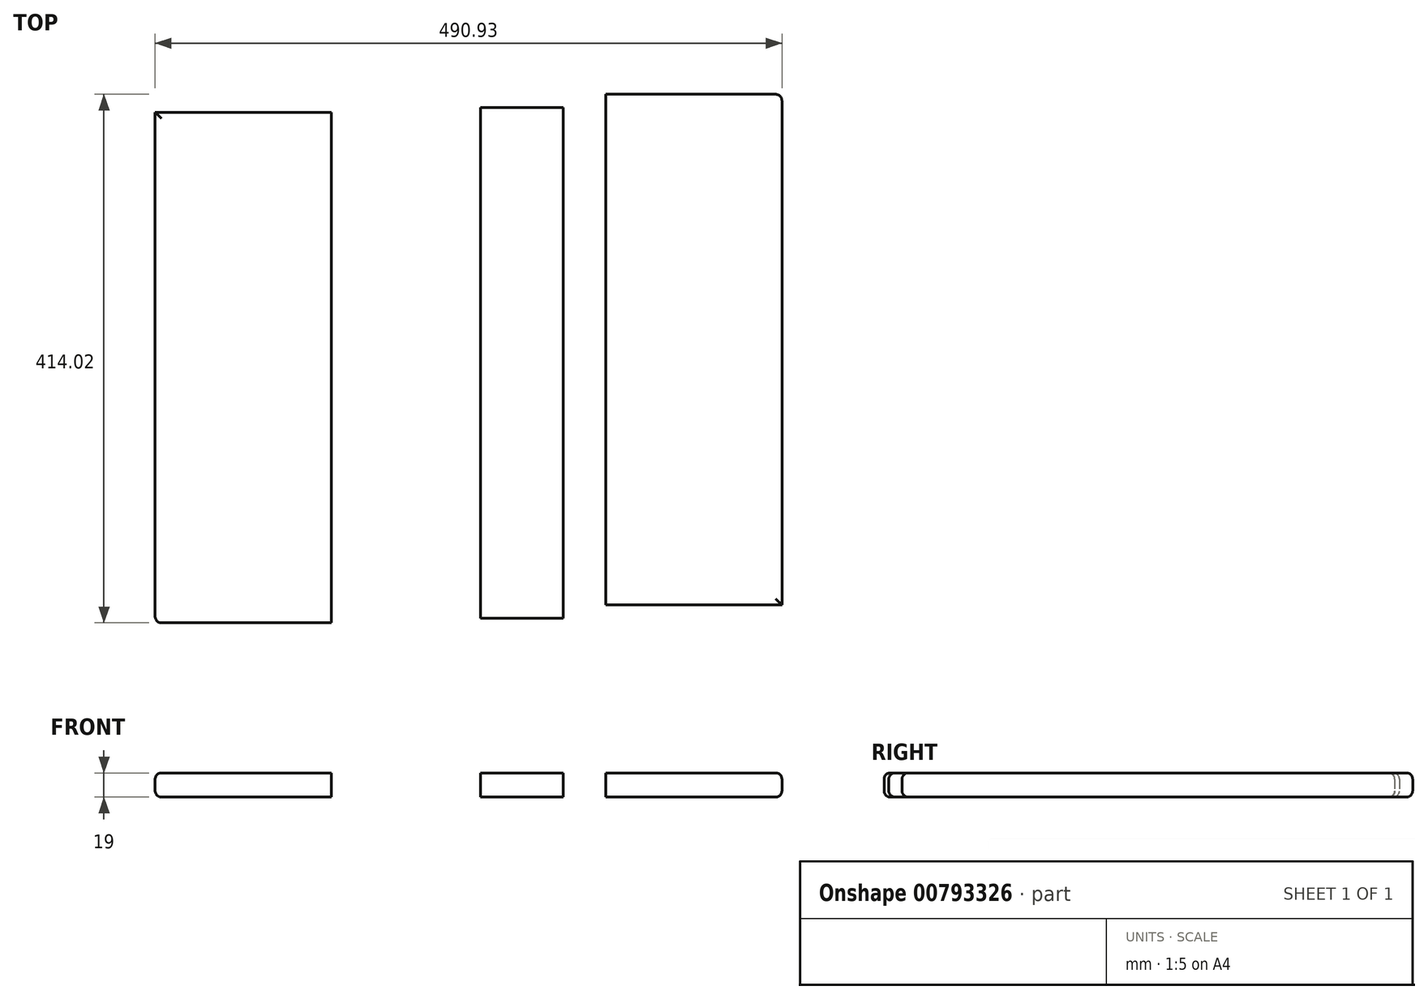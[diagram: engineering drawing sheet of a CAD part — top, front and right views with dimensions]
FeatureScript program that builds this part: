
annotation { "Feature Type Name" : "Feature", "Feature Type Description" : "" }
export const myFeature = defineFeature(function(context is Context, id is Id, definition is map)
    precondition{}
    {
        {
            var Q0;
            Q0=qCreatedBy(makeId("Top.planeOp"),FACE);
            var sketch = newSketch(context, id + "F0", { "sketchPlane" : qUnion([Q0])});
            skLineSegment(sketch, "E0.bottom", {"start": v(-196.42, 329.78) * mm, "end": v(-58.42, 329.78) * mm});
            skLineSegment(sketch, "E0.top", {"start": v(-196.42, -70.22) * mm, "end": v(-58.42, -70.22) * mm});
            skLineSegment(sketch, "E0.left", {"start": v(-196.42, 329.78) * mm, "end": v(-196.42, -70.22) * mm});
            skLineSegment(sketch, "E0.right", {"start": v(-58.42, 329.78) * mm, "end": v(-58.42, -70.22) * mm});
            skLineSegment(sketch, "E1.bottom", {"start": v(58.32, 333.43) * mm, "end": v(123.32, 333.43) * mm});
            skLineSegment(sketch, "E1.top", {"start": v(58.32, -66.57) * mm, "end": v(123.32, -66.57) * mm});
            skLineSegment(sketch, "E1.left", {"start": v(58.32, 333.43) * mm, "end": v(58.32, -66.57) * mm});
            skLineSegment(sketch, "E1.right", {"start": v(123.32, 333.43) * mm, "end": v(123.32, -66.57) * mm});
            skLineSegment(sketch, "E2.bottom", {"start": v(156.5, 343.8) * mm, "end": v(294.5, 343.8) * mm});
            skLineSegment(sketch, "E2.top", {"start": v(156.5, -56.2) * mm, "end": v(294.5, -56.2) * mm});
            skLineSegment(sketch, "E2.left", {"start": v(156.5, 343.8) * mm, "end": v(156.5, -56.2) * mm});
            skLineSegment(sketch, "E2.right", {"start": v(294.5, 343.8) * mm, "end": v(294.5, -56.2) * mm});
            skSolve(sketch);
        }
        {
            var Q0;
            Q0=makeQuery(id+"F0.imprint","IMPRINT",FACE,{"disambiguationData":[TD([[makeQuery(id+"F0.imprint","IMPRINT",EDGE,{"derivedFrom":sQuery(id+"F0.wireOp",EDGE,"E0.bottom")}),-1.0]])]});
            var Q1;
            Q1=makeQuery(id+"F0.imprint","IMPRINT",FACE,{"disambiguationData":[TD([[makeQuery(id+"F0.imprint","IMPRINT",EDGE,{"derivedFrom":sQuery(id+"F0.wireOp",EDGE,"E1.bottom")}),-1.0]])]});
            var Q2;
            Q2=makeQuery(id+"F0.imprint","IMPRINT",FACE,{"disambiguationData":[TD([[makeQuery(id+"F0.imprint","IMPRINT",EDGE,{"derivedFrom":sQuery(id+"F0.wireOp",EDGE,"E2.bottom")}),-1.0]])]});
            extrude(context, id + "F1", {"entities" : qUnion([Q0, Q1, Q2]), "depth" : 19 * mm, "offsetDistance" : 25 * mm});
        }
        {
            var Q0;
            Q0=makeQuery(id+"F1.opExtrude","CAP_EDGE",EDGE,{"disambiguationData":[OSD([sQuery(id+"F0.wireOp",EDGE,"E0.left")])],"isStart":false});
            var Q1;
            Q1=makeQuery(id+"F1.opExtrude","CAP_EDGE",EDGE,{"disambiguationData":[OSD([sQuery(id+"F0.wireOp",EDGE,"E0.bottom")])],"isStart":false});
            var Q2;
            Q2=makeQuery(id+"F1.opExtrude","CAP_EDGE",EDGE,{"disambiguationData":[OSD([sQuery(id+"F0.wireOp",EDGE,"E1.bottom")])],"isStart":false});
            var Q3;
            Q3=makeQuery(id+"F1.opExtrude","CAP_EDGE",EDGE,{"disambiguationData":[OSD([sQuery(id+"F0.wireOp",EDGE,"E2.bottom")])],"isStart":false});
            var Q4;
            Q4=makeQuery(id+"F1.opExtrude","CAP_EDGE",EDGE,{"disambiguationData":[OSD([sQuery(id+"F0.wireOp",EDGE,"E2.right")])],"isStart":true});
            var Q5;
            Q5=makeQuery(id+"F1.opExtrude","CAP_EDGE",EDGE,{"disambiguationData":[OSD([sQuery(id+"F0.wireOp",EDGE,"E2.top")])],"isStart":true});
            var Q6;
            Q6=makeQuery(id+"F1.opExtrude","CAP_EDGE",EDGE,{"disambiguationData":[OSD([sQuery(id+"F0.wireOp",EDGE,"E1.top")])],"isStart":true});
            var Q7;
            Q7=makeQuery(id+"F1.opExtrude","CAP_EDGE",EDGE,{"disambiguationData":[OSD([sQuery(id+"F0.wireOp",EDGE,"E0.top")])],"isStart":true});
            fillet(context, id + "F2", {"entities" : qUnion([Q0, Q1, Q2, Q3, Q4, Q5, Q6, Q7]), "radius" : 5 * mm, "tangentPropagation" : true, "allowEdgeOverflow" : false});
        }
        {
            var Q0;
            Q0=makeQuery(id+"F1.opExtrude","CAP_EDGE",EDGE,{"disambiguationData":[OSD([sQuery(id+"F0.wireOp",EDGE,"E0.top")])],"isStart":false});
            var Q1;
            Q1=makeQuery(id+"F1.opExtrude","CAP_EDGE",EDGE,{"disambiguationData":[OSD([sQuery(id+"F0.wireOp",EDGE,"E0.left")])],"isStart":true});
            var Q2;
            Q2=makeQuery(id+"F1.opExtrude","CAP_EDGE",EDGE,{"disambiguationData":[OSD([sQuery(id+"F0.wireOp",EDGE,"E0.bottom")])],"isStart":true});
            var Q3;
            Q3=makeQuery(id+"F1.opExtrude","CAP_EDGE",EDGE,{"disambiguationData":[OSD([sQuery(id+"F0.wireOp",EDGE,"E1.bottom")])],"isStart":true});
            var Q4;
            Q4=makeQuery(id+"F1.opExtrude","CAP_EDGE",EDGE,{"disambiguationData":[OSD([sQuery(id+"F0.wireOp",EDGE,"E1.top")])],"isStart":false});
            var Q5;
            Q5=makeQuery(id+"F1.opExtrude","CAP_EDGE",EDGE,{"disambiguationData":[OSD([sQuery(id+"F0.wireOp",EDGE,"E2.bottom")])],"isStart":true});
            var Q6;
            Q6=makeQuery(id+"F1.opExtrude","CAP_EDGE",EDGE,{"disambiguationData":[OSD([sQuery(id+"F0.wireOp",EDGE,"E2.right")])],"isStart":false});
            var Q7;
            Q7=makeQuery(id+"F1.opExtrude","CAP_EDGE",EDGE,{"disambiguationData":[OSD([sQuery(id+"F0.wireOp",EDGE,"E2.top")])],"isStart":false});
            fillet(context, id + "F3", {"entities" : qUnion([Q0, Q1, Q2, Q3, Q4, Q5, Q6, Q7]), "radius" : 5 * mm, "tangentPropagation" : true, "allowEdgeOverflow" : false});
        }
    });
